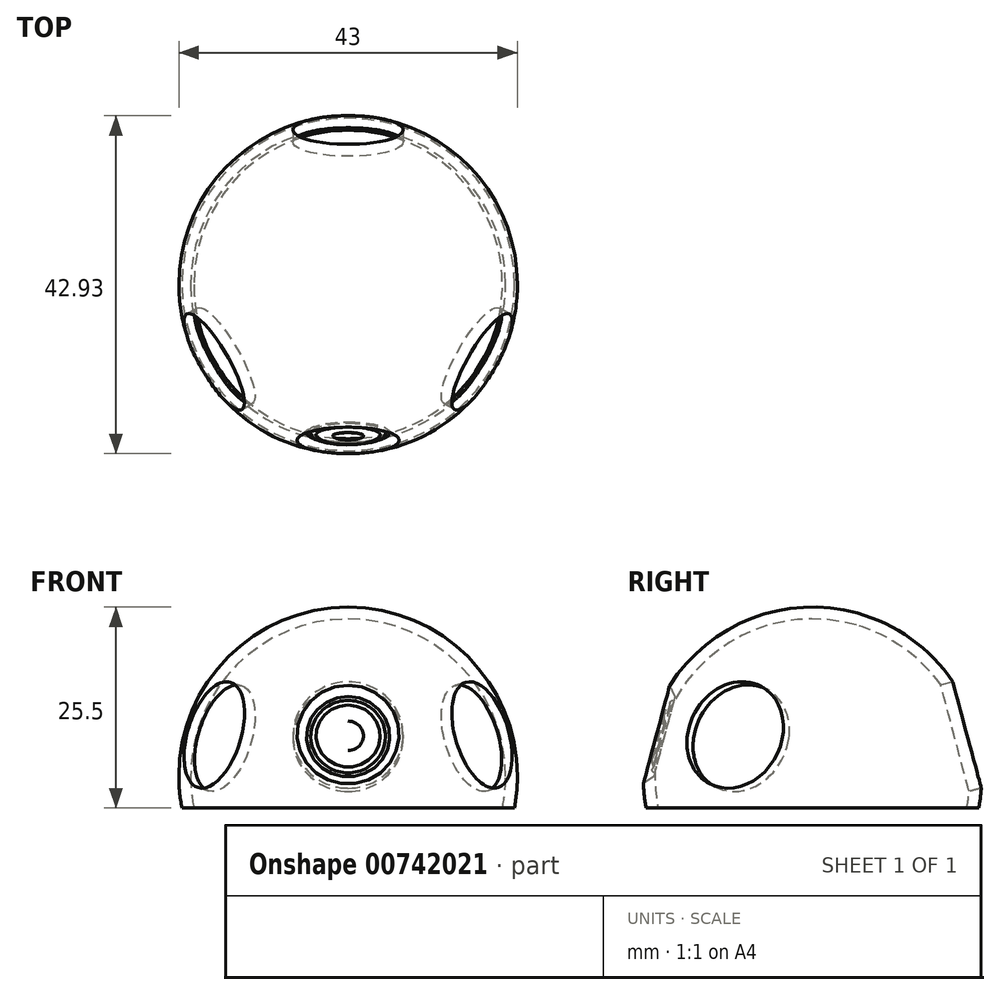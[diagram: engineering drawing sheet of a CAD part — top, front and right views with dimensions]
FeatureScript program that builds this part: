
annotation { "Feature Type Name" : "Feature", "Feature Type Description" : "" }
export const myFeature = defineFeature(function(context is Context, id is Id, definition is map)
    precondition{}
    {
        {
            var Q0;
            Q0=qCreatedBy(makeId("Top.planeOp"),FACE);
            var sketch = newSketch(context, id + "F0", { "sketchPlane" : qUnion([Q0])});
            skCircle(sketch, "E0", {"center": v(0, 0) * mm, "radius": 20 * mm});
            skLineSegment(sketch, "E1", {"start": v(-20, 0) * mm, "end": v(20, 0) * mm});
            skSolve(sketch);
        }
        {
            var Q0;
            {var subQ0=sQuery(id+"F0.wireOp",EDGE,"E1");Q0=makeQuery(id+"F0.imprint","IMPRINT",FACE,{"disambiguationData":[TD([[makeQuery(id+"F0.imprint","IMPRINT",EDGE,{"derivedFrom":subQ0}),-1.0]])]});}
            var Q1;
            Q1=sQuery(id+"F0.wireOp",EDGE,"E1");
            revolve(context, id + "F1", {"surfaceOperationType" : NewSurfaceOperationType.NEW, "entities" : qUnion([Q0]), "axis" : qUnion([Q1]), "revolveType" : RevolveType.FULL});
        }
        {
            var Q0;
            Q0=qCreatedBy(makeId("Top.planeOp"),FACE);
            var sketch = newSketch(context, id + "F2", { "sketchPlane" : qUnion([Q0])});
            skCircle(sketch, "E2", {"center": v(0, 0) * mm, "radius": 21.5 * mm});
            skLineSegment(sketch, "E3", {"start": v(-21.5, 0) * mm, "end": v(21.5, 0) * mm});
            skSolve(sketch);
        }
        {
            var Q0;
            {var subQ0=sQuery(id+"F2.wireOp",EDGE,"E3");Q0=makeQuery(id+"F2.imprint","IMPRINT",FACE,{"disambiguationData":[TD([[makeQuery(id+"F2.imprint","IMPRINT",EDGE,{"derivedFrom":subQ0}),-1.0]])]});}
            var Q1;
            Q1=sQuery(id+"F2.wireOp",EDGE,"E3");
            revolve(context, id + "F3", {"surfaceOperationType" : NewSurfaceOperationType.NEW, "entities" : qUnion([Q0]), "axis" : qUnion([Q1]), "revolveType" : RevolveType.FULL});
        }
        {
            var Q0;
            Q0=qCreatedBy(makeId("Front.planeOp"),FACE);
            var sketch = newSketch(context, id + "F4", { "sketchPlane" : qUnion([Q0])});
            skLineSegment(sketch, "E4.bottom", {"start": v(-25, -4) * mm, "end": v(25, -4) * mm});
            skLineSegment(sketch, "E4.top", {"start": v(-25, -22) * mm, "end": v(25, -22) * mm});
            skLineSegment(sketch, "E4.left", {"start": v(-25, -4) * mm, "end": v(-25, -22) * mm});
            skLineSegment(sketch, "E4.right", {"start": v(25, -4) * mm, "end": v(25, -22) * mm});
            skLineSegment(sketch, "E5", {"start": v(0, -22) * mm, "end": v(0, 0) * mm, "construction": true});
            skSolve(sketch);
        }
        {
            var Q0;
            Q0 = qSketchRegion(id + "F4", true);
            extrude(context, id + "F5", {"entities" : qUnion([Q0]), "operationType" : NewBodyOperationType.REMOVE, "endBound" : BoundingType.SYMMETRIC, "oppositeDirection" : true, "depth" : 50 * mm, "offsetDistance" : 25 * mm});
        }
        {
            var Q0;
            Q0=qCreatedBy(makeId("Top.planeOp"),FACE);
            var sketch = newSketch(context, id + "F6", { "sketchPlane" : qUnion([Q0])});
            skLineSegment(sketch, "E6", {"start": v(0, 0) * mm, "end": v(53.98, 0) * mm, "construction": true});
            skLineSegment(sketch, "E7", {"start": v(0, 0) * mm, "end": v(-32.74, 56.7) * mm, "construction": true});
            skLineSegment(sketch, "E8", {"start": v(0, 0) * mm, "end": v(-32.2, -55.76) * mm, "construction": true});
            skSolve(sketch);
        }
        {
            var Q0;
            Q0=qCreatedBy(makeId("Front.planeOp"),FACE);
            var Q1;
            Q1=sQuery(id+"F6.wireOp",EDGE,"E6");
            cPlane(context, id + "F7", {"entities" : qUnion([Q0, Q1]), "cplaneType" : CPlaneType.LINE_ANGLE, "offset" : 25 * mm, "angle" : 15 * degree, "width" : 150 * mm, "height" : 150 * mm});
        }
        {
            var Q0;
            Q0=qCreatedBy(makeId("Front.planeOp"),FACE);
            var Q1;
            Q1=sQuery(id+"F6.wireOp",EDGE,"E7");
            cPlane(context, id + "F8", {"entities" : qUnion([Q0, Q1]), "cplaneType" : CPlaneType.LINE_ANGLE, "offset" : 25 * mm, "angle" : 15 * degree, "width" : 150 * mm, "height" : 150 * mm});
        }
        {
            var Q0;
            Q0=sQuery(id+"F6.wireOp",EDGE,"E8");
            var Q1;
            Q1=qCreatedBy(makeId("Right.planeOp"),FACE);
            cPlane(context, id + "F9", {"entities" : qUnion([Q0, Q1]), "cplaneType" : CPlaneType.LINE_ANGLE, "offset" : 25 * mm, "angle" : 15 * degree, "width" : 150 * mm, "height" : 150 * mm});
        }
        {
            var Q0;
            Q0=qCreatedBy(id+"F7.planeOp",FACE);
            var sketch = newSketch(context, id + "F10", { "sketchPlane" : qUnion([Q0])});
            skCircle(sketch, "E9", {"center": v(0, 0) * mm, "radius": 7 * mm});
            skSolve(sketch);
        }
        {
            var Q0;
            Q0 = qSketchRegion(id + "F10", true);
            var Q1;
            Q1=makeQuery(id+"F3.opRevolve","SWEPT_FACE",FACE,{"disambiguationData":[OSD([sQuery(id+"F2.wireOp",EDGE,"E2")])]});
            extrude(context, id + "F11", {"entities" : qUnion([Q0]), "operationType" : NewBodyOperationType.REMOVE, "endBound" : BoundingType.UP_TO_SURFACE, "depth" : 25 * mm, "endBoundEntityFace" : qUnion([Q1]), "offsetDistance" : 25 * mm});
        }
        {
            var Q0;
            Q0=qCreatedBy(id+"F8.planeOp",FACE);
            var sketch = newSketch(context, id + "F12", { "sketchPlane" : qUnion([Q0])});
            skCircle(sketch, "E10", {"center": v(0, 0) * mm, "radius": 7 * mm});
            skSolve(sketch);
        }
        {
            var Q0;
            Q0 = qSketchRegion(id + "F12", true);
            var Q1;
            Q1=makeQuery(id+"F3.opRevolve","SWEPT_FACE",FACE,{"disambiguationData":[OSD([sQuery(id+"F2.wireOp",EDGE,"E2")])]});
            extrude(context, id + "F13", {"entities" : qUnion([Q0]), "operationType" : NewBodyOperationType.REMOVE, "endBound" : BoundingType.UP_TO_SURFACE, "oppositeDirection" : true, "depth" : 25 * mm, "endBoundEntityFace" : qUnion([Q1]), "offsetDistance" : 25 * mm});
        }
        {
            var Q0;
            Q0=qCreatedBy(id+"F9.planeOp",FACE);
            var sketch = newSketch(context, id + "F14", { "sketchPlane" : qUnion([Q0])});
            skCircle(sketch, "E11", {"center": v(0, 0) * mm, "radius": 7 * mm});
            skSolve(sketch);
        }
        {
            var Q0;
            Q0 = qSketchRegion(id + "F14", true);
            var Q1;
            Q1=makeQuery(id+"F3.opRevolve","SWEPT_FACE",FACE,{"disambiguationData":[OSD([sQuery(id+"F2.wireOp",EDGE,"E2")])]});
            extrude(context, id + "F15", {"entities" : qUnion([Q0]), "operationType" : NewBodyOperationType.REMOVE, "endBound" : BoundingType.UP_TO_SURFACE, "oppositeDirection" : true, "depth" : 25 * mm, "endBoundEntityFace" : qUnion([Q1]), "offsetDistance" : 25 * mm});
        }
        {
            var Q0;
            Q0=qCreatedBy(makeId("Front.planeOp"),FACE);
            var Q1;
            Q1=sQuery(id+"F6.wireOp",EDGE,"E6");
            cPlane(context, id + "F16", {"entities" : qUnion([Q0, Q1]), "cplaneType" : CPlaneType.LINE_ANGLE, "offset" : 25 * mm, "angle" : 345 * degree, "width" : 150 * mm, "height" : 150 * mm});
        }
        {
            var Q0;
            Q0=qCreatedBy(id+"F16.planeOp",FACE);
            var sketch = newSketch(context, id + "F17", { "sketchPlane" : qUnion([Q0])});
            skCircle(sketch, "E12", {"center": v(0, 0) * mm, "radius": 6.5 * mm});
            skSolve(sketch);
        }
        {
            var Q0;
            Q0 = qSketchRegion(id + "F17", true);
            extrude(context, id + "F18", {"entities" : qUnion([Q0]), "operationType" : NewBodyOperationType.REMOVE, "oppositeDirection" : true, "depth" : 30 * mm, "offsetDistance" : 25 * mm, "hasSecondDirection" : true, "secondDirectionOppositeDirection" : true, "secondDirectionDepth" : 20.5 * mm});
        }
        {
            var Q0;
            Q0=makeQuery(id+"F18.boolean.opBoolean","COPY",FACE,{"derivedFrom":makeQuery(id+"F18.opExtrude","CAP_FACE",FACE,{"disambiguationData":[OSD([sQuery(id+"F17.wireOp",EDGE,"E12")])],"isStart":true})});
            extrude(context, id + "F19", {"entities" : qUnion([Q0]), "operationType" : NewBodyOperationType.REMOVE, "oppositeDirection" : true, "depth" : 1 * mm, "offsetDistance" : 25 * mm, "hasDraft" : true, "draftAngle" : 50 * degree, "draftPullDirection" : true});
        }
        {
            var Q0;
            Q0=sQuery(id+"F6.wireOp",EDGE,"E6");
            var Q1;
            Q1=makeQuery(id+"F19.boolean.opBoolean","INTERSECT",EDGE,{"derivedFrom":[makeQuery(id+"F1.opRevolve","SWEPT_FACE",FACE,{"disambiguationData":[OSD([sQuery(id+"F0.wireOp",EDGE,"E0")])]}),makeQuery(id+"F19.opExtrude","CAP_FACE",FACE,{"disambiguationData":[OSD([sQuery(id+"F17.wireOp",EDGE,"E12")])],"isStart":false})]});
            cPlane(context, id + "F20", {"entities" : qUnion([Q0, Q1]), "cplaneType" : CPlaneType.LINE_ANGLE, "offset" : 25 * mm, "angle" : 0 * degree, "width" : 150 * mm, "height" : 150 * mm});
        }
        {
            var Q0;
            Q0=qCreatedBy(id+"F20.planeOp",FACE);
            var sketch = newSketch(context, id + "F21", { "sketchPlane" : qUnion([Q0])});
            skLineSegment(sketch, "E13.0", {"start": v(5.29, -19.5) * mm, "end": v(-5.29, -19.5) * mm});
            skCircle(sketch, "E14", {"center": v(0, -19.5) * mm, "radius": 0.75 * mm});
            skArc(sketch, "E15", {"start": v(1.5, -19.5) * mm, "mid": v(2.92, -20.2) * mm, "end": v(4.35, -19.5) * mm});
            skCircle(sketch, "E16", {"center": v(1.5, -19.5) * mm, "radius": 0.4 * mm});
            skCircle(sketch, "E17", {"center": v(4.35, -19.5) * mm, "radius": 0.4 * mm});
            skLineSegment(sketch, "E18", {"start": v(0, 0) * mm, "end": v(0, -19.5) * mm, "construction": true});
            skLineSegment(sketch, "E19", {"start": v(0, -18.75) * mm, "end": v(0, -20.25) * mm});
            skSolve(sketch);
        }
        {
            var Q0;
            {var subQ0=sQuery(id+"F21.wireOp",EDGE,"E15");var subQ1=sQuery(id+"F21.wireOp",EDGE,"E13.0");var subQ2=makeQuery(id+"F21.imprint","INTERSECT",VERTEX,{"disambiguationData":[OD(1.0)],"derivedFrom":[subQ1,subQ0]});Q0=makeQuery(id+"F21.imprint","IMPRINT",FACE,{"disambiguationData":[TD([[makeQuery(id+"F21.imprint","IMPRINT",EDGE,{"disambiguationData":[TD([[subQ2,1.0]])],"derivedFrom":subQ1}),1.0]])]});}
            var Q1;
            {var subQ0=sQuery(id+"F21.wireOp",EDGE,"E15");var subQ1=sQuery(id+"F21.wireOp",EDGE,"E13.0");var subQ2=makeQuery(id+"F21.imprint","INTERSECT",VERTEX,{"disambiguationData":[OD(1.0)],"derivedFrom":[subQ1,subQ0]});Q1=makeQuery(id+"F21.imprint","IMPRINT",FACE,{"disambiguationData":[TD([[makeQuery(id+"F21.imprint","IMPRINT",EDGE,{"disambiguationData":[TD([[subQ2,-1.0]])],"derivedFrom":subQ1}),1.0]])]});}
            var Q2;
            {var subQ0=sQuery(id+"F21.wireOp",EDGE,"E17");var subQ1=sQuery(id+"F21.wireOp",EDGE,"E13.0");var subQ2=makeQuery(id+"F21.imprint","INTERSECT",VERTEX,{"disambiguationData":[OD(1.0)],"derivedFrom":[subQ1,subQ0]});Q2=makeQuery(id+"F21.imprint","IMPRINT",FACE,{"disambiguationData":[TD([[makeQuery(id+"F21.imprint","IMPRINT",EDGE,{"disambiguationData":[TD([[subQ2,-1.0]])],"derivedFrom":subQ1}),1.0]])]});}
            var Q3;
            {var subQ0=sQuery(id+"F21.wireOp",EDGE,"E15");var subQ1=sQuery(id+"F21.wireOp",EDGE,"E13.0");var subQ2=makeQuery(id+"F21.imprint","INTERSECT",VERTEX,{"disambiguationData":[OD(0.0)],"derivedFrom":[subQ1,subQ0]});Q3=makeQuery(id+"F21.imprint","IMPRINT",FACE,{"disambiguationData":[TD([[makeQuery(id+"F21.imprint","IMPRINT",EDGE,{"disambiguationData":[TD([[subQ2,1.0]])],"derivedFrom":subQ1}),1.0]])]});}
            var Q4;
            {var subQ0=sQuery(id+"F21.wireOp",EDGE,"E15");var subQ1=sQuery(id+"F21.wireOp",EDGE,"E13.0");var subQ2=makeQuery(id+"F21.imprint","INTERSECT",VERTEX,{"disambiguationData":[OD(0.0)],"derivedFrom":[subQ1,subQ0]});Q4=makeQuery(id+"F21.imprint","IMPRINT",FACE,{"disambiguationData":[TD([[makeQuery(id+"F21.imprint","IMPRINT",EDGE,{"disambiguationData":[TD([[subQ2,-1.0]])],"derivedFrom":subQ1}),1.0]])]});}
            var Q5;
            {var subQ0=sQuery(id+"F21.wireOp",EDGE,"E14");var subQ1=sQuery(id+"F21.wireOp",EDGE,"E13.0");var subQ2=makeQuery(id+"F21.imprint","INTERSECT",VERTEX,{"disambiguationData":[OD(0.0)],"derivedFrom":[subQ1,subQ0]});Q5=makeQuery(id+"F21.imprint","IMPRINT",FACE,{"disambiguationData":[TD([[makeQuery(id+"F21.imprint","IMPRINT",EDGE,{"disambiguationData":[TD([[subQ2,-1.0]])],"derivedFrom":subQ1}),1.0]])]});}
            var Q6;
            Q6=sQuery(id+"F21.wireOp",EDGE,"E18");
            revolve(context, id + "F22", {"operationType" : NewBodyOperationType.ADD, "surfaceOperationType" : NewSurfaceOperationType.NEW, "entities" : qUnion([Q0, Q1, Q2, Q3, Q4, Q5]), "axis" : qUnion([Q6]), "revolveType" : RevolveType.FULL});
        }
        {
            var Q0;
            Q0=qCreatedBy(makeId("Top.planeOp"),FACE);
            var sketch = newSketch(context, id + "F23", { "sketchPlane" : qUnion([Q0])});
            skLineSegment(sketch, "E20", {"start": v(-20, 0) * mm, "end": v(20, 0) * mm});
            skArc(sketch, "E21", {"start": v(-20, 0) * mm, "mid": v(0, -20) * mm, "end": v(20, 0) * mm});
            skSolve(sketch);
        }
        {
            var Q0;
            Q0 = qSketchRegion(id + "F23", true);
            var Q1;
            Q1=sQuery(id+"F0.wireOp",EDGE,"E1");
            revolve(context, id + "F24", {"operationType" : NewBodyOperationType.REMOVE, "surfaceOperationType" : NewSurfaceOperationType.NEW, "entities" : qUnion([Q0]), "axis" : qUnion([Q1]), "revolveType" : RevolveType.FULL, "oppositeDirection" : true});
        }
    });
